# Revit family: ledfloodoly-p_re600-800w-740-as-lum_709000083800
name_source: partatom
category: Leuchten
revit_build: Autodesk Revit 2016 (Build: 20190508_0715(x64)
units: mm (PartAtom-declared; Revit-internal decimal feet)

## family parameters
Basisbauteil = Fläche
Beim Laden mit Abzugskörper schneiden = Nein
Bemaßung runder Anschluss = Durchmesser verwenden
Gemeinsam genutzt = Nein
Lichtquelle = Nein
Raumberechnungspunkt = Nein
Teiletyp = Normal

## types (1)
- LEDFloodOly-P Re600-800W-740-AS-LUM (1 x LED, 120000 lm, 4000)
    Approval mark = CE, ENEC
    Beschreibung = Professional luminaire with die-cast aluminium body for sports and area lighting. Flexible driver mounting methods. Robust design: full IP66 and IK08 protection, including safety cable. Equipped with DALI dimming for further energy saving. Equipped with b
    CIE Flux Codes = 58 94 100 100 100
    Color Rendering = 70
    Color Temperature = 4000
    Control Gear = Electronic ballast
    Frequency = 60 Hz
    Height = 356 mm
    Hersteller = OPPLE
    Lamp Light Flux = 120000 lm
    Lamp count = 1
    Lampe = 1 x LED
    Length = 607 mm
    Luminous efficacy = 150 lm/W
    ModVariant = Nein
    Modell = 709000083800
    Mounting Place = Pole
    Mounting Type = Pole top
    Number of Poles = 1
    OnlyDefault = Ja
    Power Factor = 1
    Product Name = LEDFloodOly-P Re600-800W-740-AS-LUM
    Product group = Filament A60
    ProductGroupID = 310
    Protection Class = Protection class I
    Protection Degree = IP 66
    RLX_Detail_Level = 1
    RlxData = <blob elided: 227725 chars, md5=99d5cf41>
    Scheinlast = 800 VA
    Socket = socket
    Standby Power = 0 W
    System Light Flux = 120000 lm
    System Power = 800 W
    Typenbild = web_fl_olympus_re600_v4.jpg
    Typenkommentare = Product without accessories
    URL = http://relux.com
    VarID = ---
    Voltage = 230 V
    Voltage Range = 220-240 V
    Vorgabe-Ansicht = 1800 mm
    Weight = 0.00 kg
    Width = 612 mm

## geometry (parser evidence)
native form markers: Blend x4, Sweep x15
no freeform markers — native parametric forms only
